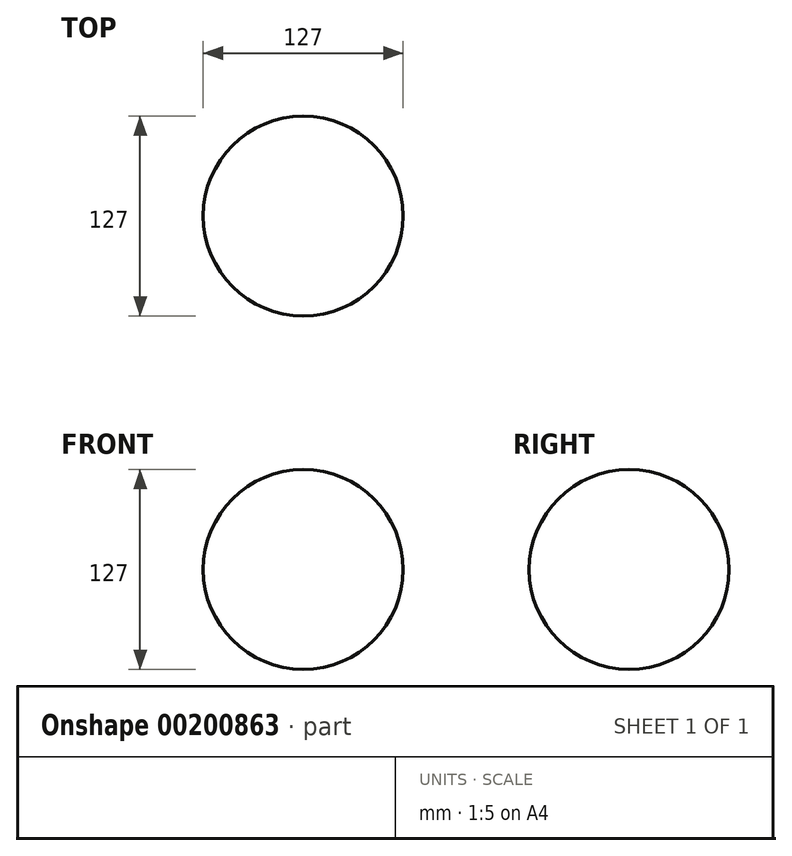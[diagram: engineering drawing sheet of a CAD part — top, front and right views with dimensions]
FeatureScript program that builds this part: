
annotation { "Feature Type Name" : "Feature", "Feature Type Description" : "" }
export const myFeature = defineFeature(function(context is Context, id is Id, definition is map)
    precondition{}
    {
        {
            var Q0;
            Q0=qCreatedBy(makeId("Front.planeOp"),FACE);
            var sketch = newSketch(context, id + "F0", { "sketchPlane" : qUnion([Q0])});
            skArc(sketch, "E0", {"start": v(-10.54, 63.99) * mm, "mid": v(-74.04, 0.49) * mm, "end": v(-10.54, -63.01) * mm});
            skLineSegment(sketch, "E1", {"start": v(-10.54, 63.99) * mm, "end": v(-10.54, -63.01) * mm});
            skSolve(sketch);
        }
        {
            var Q0;
            Q0=makeQuery(id+"F0.imprint","IMPRINT",FACE,{"disambiguationData":[TD([[makeQuery(id+"F0.imprint","IMPRINT",EDGE,{"derivedFrom":sQuery(id+"F0.wireOp",EDGE,"E0")}),1.0]])]});
            var Q1;
            Q1=sQuery(id+"F0.wireOp",EDGE,"E1");
            revolve(context, id + "F1", {"entities" : qUnion([Q0]), "axis" : qUnion([Q1]), "revolveType" : RevolveType.FULL});
        }
    });
